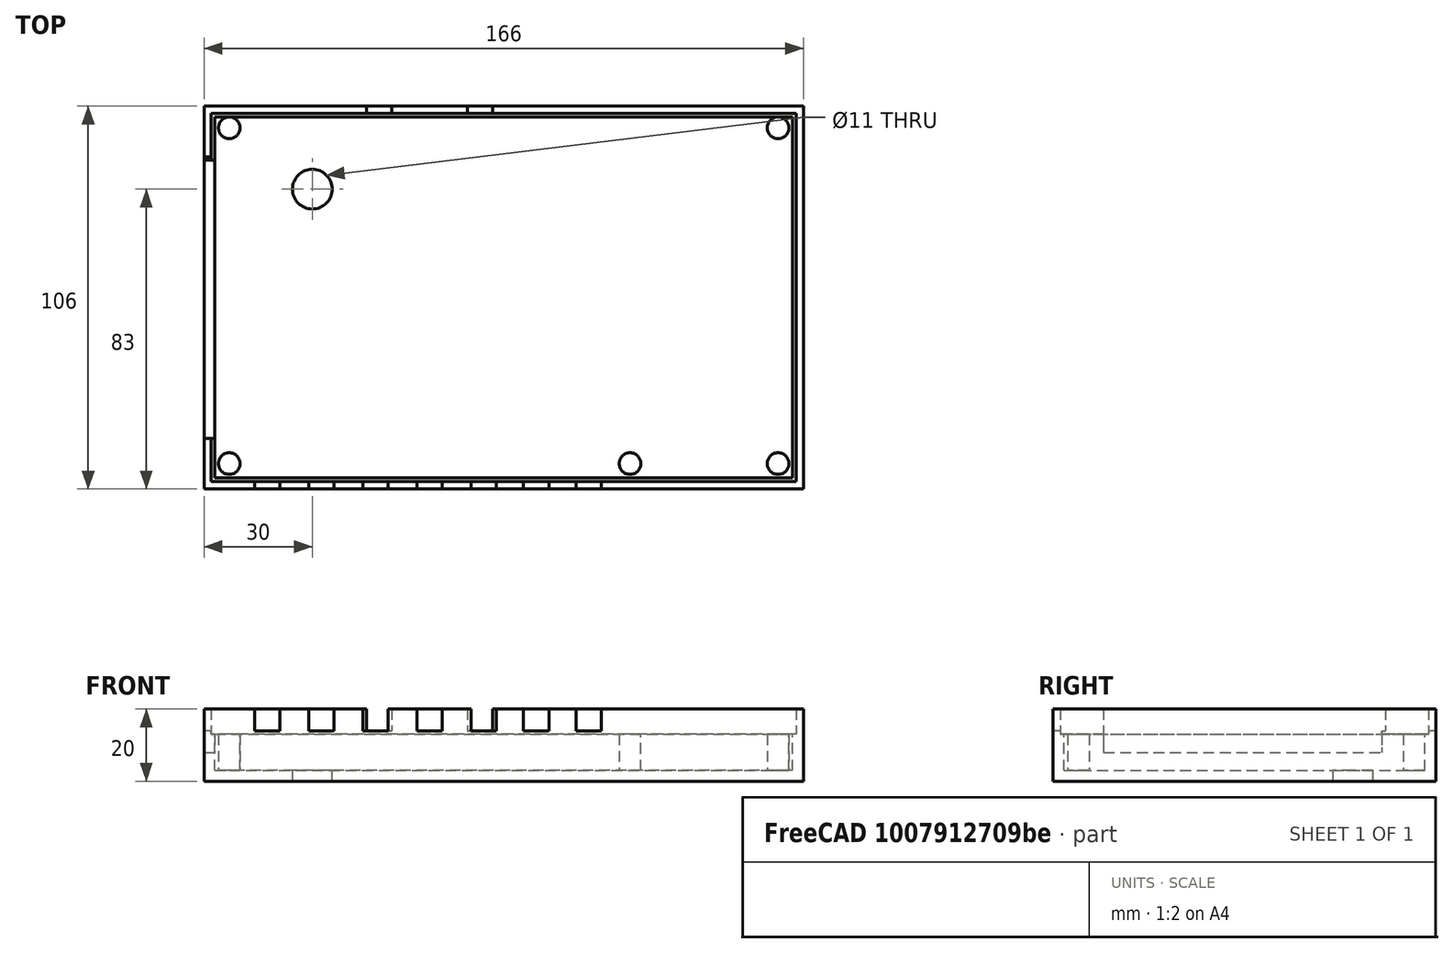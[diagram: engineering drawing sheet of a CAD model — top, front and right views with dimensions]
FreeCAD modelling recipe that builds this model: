
FCSTD DOCUMENT  (FreeCAD 1.0R39319 (Git))
Label: PLC14500-Nano-SupportV2
License: All rights reserved
LicenseURL: http://en.wikipedia.org/wiki/All_rights_reserved
objects: Sketcher::SketchObject×8, PartDesign::Pocket×5, PartDesign::Pad×3, App::DocumentObjectGroup×1, PartDesign::Body×1
note: 41 computed .brp shape members not serialized (recipe doc carries the construction recipe); baked Part::Feature solids carry a one-line shape summary decoded from their .brp

FEATURE [Sketcher::SketchObject] Sketch
  ArcFitTolerance = 0
  AttachmentSupport = -> [XY_Plane]
  FullyConstrained = true
  MakeInternals = false
  MapMode = 5
  sketch-geometry (4):
    g0: LineSegment StartX=-80 StartY=50 StartZ=0 EndX=80 EndY=50 EndZ=0
    g1: LineSegment StartX=80 StartY=50 StartZ=0 EndX=80 EndY=-50 EndZ=0
    g2: LineSegment StartX=80 StartY=-50 StartZ=0 EndX=-80 EndY=-50 EndZ=0
    g3: LineSegment StartX=-80 StartY=-50 StartZ=0 EndX=-80 EndY=50 EndZ=0
  constraints (10):
    c: Coincident(g0,g1)
    c: Coincident(g1,g2)
    c: Coincident(g2,g3)
    c: Coincident(g3,g0)
    c: Horizontal(g2)
    c: Vertical(g3)
    c: DistanceX(g0,g0) = 160
    c: DistanceY(g1,g1) = 100
    c: Symmetric(g0,g0,g-2)
    c: Symmetric(g0,g1,g-1)
FEATURE [PartDesign::Pad] Pad  label="Plate"
  Direction = (0,0,1)
  Length = 3
  Length2 = 100
  Profile = -> Sketch
  Suppressed = false
  Type = 0
FEATURE [Sketcher::SketchObject] Sketch001
  ArcFitTolerance = 0
  AttachmentSupport = -> [Pad]
  ExternalGeometry = -> [Pad]
  FullyConstrained = true
  MakeInternals = false
  MapMode = 5
  Placement = pos=(0,0,3) rot=(0,0,1;0rad)
  sketch-geometry (5):
    g0: Circle CenterX=-76 CenterY=47 CenterZ=0 NormalX=0 NormalY=0 NormalZ=1 AngleXU=0 Radius=3
    g1: Circle CenterX=76 CenterY=47 CenterZ=0 NormalX=0 NormalY=0 NormalZ=1 AngleXU=0 Radius=3
    g2: Circle CenterX=76 CenterY=-46 CenterZ=0 NormalX=0 NormalY=0 NormalZ=1 AngleXU=0 Radius=3
    g3: Circle CenterX=-76 CenterY=-46 CenterZ=0 NormalX=0 NormalY=0 NormalZ=1 AngleXU=0 Radius=3
    g4: Circle CenterX=35 CenterY=-46 CenterZ=0 NormalX=0 NormalY=0 NormalZ=1 AngleXU=0 Radius=3
  constraints (15):
    c: DistanceX(g-6,g0) = 4
    c: DistanceY(g0,g-6) = 3
    c: Radius(g0) = 3
    c: DistanceX(g1,g-4) = 4
    c: DistanceY(g1,g-4) = 3
    c: Radius(g1) = 3
    c: DistanceX(g2,g1) = 0
    c: DistanceX(g0,g3) = 0
    c: DistanceY(g-6,g3) = 4
    c: DistanceY(g-6,g4) = 4
    c: DistanceY(g-5,g2) = 4
    c: Radius(g3) = 3
    c: Radius(g4) = 3
    c: Radius(g2) = 3
    c: DistanceX(g4,g2) = 41
FEATURE [PartDesign::Pad] Pad001  label="BoardSupports"
  BaseFeature = -> Pad
  Direction = (0,0,1)
  Length = 10
  Length2 = 100
  Profile = -> Sketch001
  Suppressed = false
  Type = 0
FEATURE [Sketcher::SketchObject] Sketch002
  ArcFitTolerance = 1e-06
  AttachmentSupport = -> [XY_Plane]
  ExternalGeometry = -> [Pad001]
  FullyConstrained = true
  MakeInternals = false
  MapMode = 5
  sketch-geometry (8):
    g0: LineSegment StartX=-80 StartY=50 StartZ=0 EndX=-80 EndY=-50 EndZ=0
    g1: LineSegment StartX=-80 StartY=-50 StartZ=0 EndX=80 EndY=-50 EndZ=0
    g2: LineSegment StartX=80 StartY=-50 StartZ=0 EndX=80 EndY=50 EndZ=0
    g3: LineSegment StartX=80 StartY=50 StartZ=0 EndX=-80 EndY=50 EndZ=0
    g4: LineSegment StartX=-83 StartY=53 StartZ=0 EndX=-83 EndY=-53 EndZ=0
    g5: LineSegment StartX=-83 StartY=-53 StartZ=0 EndX=83 EndY=-53 EndZ=0
    g6: LineSegment StartX=83 StartY=-53 StartZ=0 EndX=83 EndY=53 EndZ=0
    g7: LineSegment StartX=83 StartY=53 StartZ=0 EndX=-83 EndY=53 EndZ=0
  constraints (22):
    c: Coincident(g0,g1)
    c: Coincident(g1,g2)
    c: Coincident(g2,g3)
    c: Coincident(g3,g0)
    c: Vertical(g0)
    c: Vertical(g2)
    c: Horizontal(g1)
    c: Horizontal(g3)
    c: Coincident(g2,g-3)
    c: Coincident(g0,g-5)
    c: Coincident(g4,g5)
    c: Coincident(g5,g6)
    c: Coincident(g6,g7)
    c: Coincident(g7,g4)
    c: Vertical(g4)
    c: Vertical(g6)
    c: Horizontal(g5)
    c: Horizontal(g7)
    c: DistanceY(g2,g6) = 3
    c: DistanceY(g5,g1) = 3
    c: DistanceX(g1,g5) = 3
    c: DistanceX(g4,g0) = 3
FEATURE [PartDesign::Pad] Pad002  label="Walls"
  BaseFeature = -> Pad001
  Direction = (0,0,1)
  Length = 20
  Length2 = 10
  Profile = -> Sketch002
  ReferenceAxis = -> Sketch002 [N_Axis]
  Refine = true
  Suppressed = false
  Type = 0
FEATURE [Sketcher::SketchObject] Sketch003
  ArcFitTolerance = 1e-06
  AttachmentOffset = pos=(0,0,20) rot=(0,0,1;0rad)
  AttachmentSupport = -> [XY_Plane]
  ExternalGeometry = -> [Pad002]
  FullyConstrained = true
  MakeInternals = false
  MapMode = 5
  Placement = pos=(0,0,20) rot=(0,0,1;0rad)
  sketch-geometry (40):
    g0: LineSegment StartX=-69 StartY=-51 StartZ=0 EndX=-69 EndY=-53 EndZ=0
    g1: LineSegment StartX=-69 StartY=-53 StartZ=0 EndX=-62 EndY=-53 EndZ=0
    g2: LineSegment StartX=-62 StartY=-53 StartZ=0 EndX=-62 EndY=-51 EndZ=0
    g3: LineSegment StartX=-62 StartY=-51 StartZ=0 EndX=-69 EndY=-51 EndZ=0
    g4: LineSegment StartX=-54 StartY=-51 StartZ=0 EndX=-54 EndY=-53 EndZ=0
    g5: LineSegment StartX=-54 StartY=-53 StartZ=0 EndX=-47 EndY=-53 EndZ=0
    g6: LineSegment StartX=-47 StartY=-53 StartZ=0 EndX=-47 EndY=-51 EndZ=0
    g7: LineSegment StartX=-47 StartY=-51 StartZ=0 EndX=-54 EndY=-51 EndZ=0
    g8: LineSegment StartX=-39 StartY=-51 StartZ=0 EndX=-39 EndY=-53 EndZ=0
    g9: LineSegment StartX=-39 StartY=-53 StartZ=0 EndX=-32 EndY=-53 EndZ=0
    g10: LineSegment StartX=-32 StartY=-53 StartZ=0 EndX=-32 EndY=-51 EndZ=0
    g11: LineSegment StartX=-32 StartY=-51 StartZ=0 EndX=-39 EndY=-51 EndZ=0
    g12: LineSegment StartX=-24 StartY=-51 StartZ=0 EndX=-24 EndY=-53 EndZ=0
    g13: LineSegment StartX=-24 StartY=-53 StartZ=0 EndX=-17 EndY=-53 EndZ=0
    g14: LineSegment StartX=-17 StartY=-53 StartZ=0 EndX=-17 EndY=-51 EndZ=0
    g15: LineSegment StartX=-17 StartY=-51 StartZ=0 EndX=-24 EndY=-51 EndZ=0
    g16: LineSegment StartX=-9 StartY=-51 StartZ=0 EndX=-9 EndY=-53 EndZ=0
    g17: LineSegment StartX=-9 StartY=-53 StartZ=0 EndX=-2 EndY=-53 EndZ=0
    g18: LineSegment StartX=-2 StartY=-53 StartZ=0 EndX=-2 EndY=-51 EndZ=0
    g19: LineSegment StartX=-2 StartY=-51 StartZ=0 EndX=-9 EndY=-51 EndZ=0
    g20: LineSegment StartX=5.5 StartY=-51 StartZ=0 EndX=5.5 EndY=-53 EndZ=0
    g21: LineSegment StartX=5.5 StartY=-53 StartZ=0 EndX=12.5 EndY=-53 EndZ=0
    g22: LineSegment StartX=12.5 StartY=-53 StartZ=0 EndX=12.5 EndY=-51 EndZ=0
    g23: LineSegment StartX=12.5 StartY=-51 StartZ=0 EndX=5.5 EndY=-51 EndZ=0
    g24: LineSegment StartX=20 StartY=-51 StartZ=0 EndX=20 EndY=-53 EndZ=0
    g25: LineSegment StartX=20 StartY=-53 StartZ=0 EndX=27 EndY=-53 EndZ=0
    g26: LineSegment StartX=27 StartY=-53 StartZ=0 EndX=27 EndY=-51 EndZ=0
    g27: LineSegment StartX=27 StartY=-51 StartZ=0 EndX=20 EndY=-51 EndZ=0
    g28: LineSegment StartX=-37 StartY=51 StartZ=0 EndX=-37 EndY=53 EndZ=0
    g29: LineSegment StartX=-37 StartY=53 StartZ=0 EndX=-30 EndY=53 EndZ=0
    g30: LineSegment StartX=-30 StartY=53 StartZ=0 EndX=-30 EndY=51 EndZ=0
    g31: LineSegment StartX=-30 StartY=51 StartZ=0 EndX=-37 EndY=51 EndZ=0
    g32: LineSegment StartX=-10 StartY=51 StartZ=0 EndX=-10 EndY=53 EndZ=0
    g33: LineSegment StartX=-10 StartY=53 StartZ=0 EndX=-3 EndY=53 EndZ=0
    g34: LineSegment StartX=-3 StartY=53 StartZ=0 EndX=-3 EndY=51 EndZ=0
    g35: LineSegment StartX=-3 StartY=51 StartZ=0 EndX=-10 EndY=51 EndZ=0
    g36: LineSegment StartX=-83 StartY=39 StartZ=0 EndX=-83 EndY=-39 EndZ=0
    g37: LineSegment StartX=-83 StartY=-39 StartZ=0 EndX=-81 EndY=-39 EndZ=0
    g38: LineSegment StartX=-81 StartY=-39 StartZ=0 EndX=-81 EndY=39 EndZ=0
    g39: LineSegment StartX=-81 StartY=39 StartZ=0 EndX=-83 EndY=39 EndZ=0
  constraints (120):
    c: Coincident(g0,g1)
    c: Coincident(g1,g2)
    c: Coincident(g2,g3)
    c: Coincident(g3,g0)
    c: Vertical(g0)
    c: Vertical(g2)
    c: Horizontal(g1)
    c: Horizontal(g3)
    c: DistanceX(g3,g3) = 7
    c: DistanceY(g2,g2) = 2
    c: DistanceX(g-5,g0) = 14
    c: PointOnObject(g0,g-3)
    c: Coincident(g4,g5)
    c: Coincident(g5,g6)
    c: Coincident(g6,g7)
    c: Coincident(g7,g4)
    c: Vertical(g4)
    c: Vertical(g6)
    c: Horizontal(g5)
    c: Horizontal(g7)
    c: Coincident(g8,g9)
    c: Coincident(g9,g10)
    c: Coincident(g10,g11)
    c: Coincident(g11,g8)
    c: Vertical(g8)
    c: Vertical(g10)
    c: Horizontal(g9)
    c: Horizontal(g11)
    c: Coincident(g12,g13)
    c: Coincident(g13,g14)
    c: Coincident(g14,g15)
    c: Coincident(g15,g12)
    c: Vertical(g12)
    c: Vertical(g14)
    c: Horizontal(g13)
    c: Horizontal(g15)
    c: Coincident(g16,g17)
    c: Coincident(g17,g18)
    c: Coincident(g18,g19)
    c: Coincident(g19,g16)
    c: Vertical(g16)
    c: Vertical(g18)
    c: Horizontal(g17)
    c: Horizontal(g19)
    c: Coincident(g20,g21)
    c: Coincident(g21,g22)
    c: Coincident(g22,g23)
    c: Coincident(g23,g20)
    c: Vertical(g20)
    c: Vertical(g22)
    c: Horizontal(g21)
    c: Horizontal(g23)
    c: Coincident(g24,g25)
    c: Coincident(g25,g26)
    c: Coincident(g26,g27)
    c: Coincident(g27,g24)
    c: Vertical(g24)
    c: Vertical(g26)
    c: Horizontal(g25)
    c: Horizontal(g27)
    c: Equal(g3,g7)
    c: Equal(g7,g11)
    c: Equal(g11,g15)
    c: Equal(g15,g19)
    c: Equal(g19,g23)
    c: Equal(g23,g27)
    c: Equal(g2,g4)
    c: Equal(g6,g8)
    c: Equal(g10,g12)
    c: Equal(g14,g16)
    c: Equal(g18,g20)
    c: PointOnObject(g4,g-3)
    c: PointOnObject(g8,g-3)
    c: PointOnObject(g12,g-3)
    c: PointOnObject(g16,g-3)
    c: PointOnObject(g20,g-3)
    c: PointOnObject(g24,g-3)
    c: Equal(g22,g24)
    c: DistanceX(g1,g5) = 15
    c: DistanceX(g5,g9) = 15
    c: DistanceX(g9,g13) = 15
    c: DistanceX(g13,g17) = 15
    c: DistanceX(g17,g21) = 14.5
    c: DistanceX(g21,g25) = 14.5
    c: Coincident(g28,g29)
    c: Coincident(g29,g30)
    c: Coincident(g30,g31)
    c: Coincident(g31,g28)
    c: Vertical(g28)
    c: Vertical(g30)
    c: Horizontal(g29)
    c: Horizontal(g31)
    c: Coincident(g32,g33)
    c: Coincident(g33,g34)
    c: Coincident(g34,g35)
    c: Coincident(g35,g32)
    c: Vertical(g32)
    c: Vertical(g34)
    c: Horizontal(g33)
    c: Horizontal(g35)
    c: Equal(g7,g29)
    c: Equal(g29,g33)
    c: Equal(g30,g32)
    c: Equal(g4,g28)
    c: DistanceX(g-6,g28) = 46
    c: DistanceX(g28,g32) = 27
    c: Coincident(g36,g37)
    c: Coincident(g37,g38)
    c: Coincident(g38,g39)
    c: Coincident(g39,g36)
    c: Vertical(g36)
    c: Vertical(g38)
    c: Horizontal(g37)
    c: Horizontal(g39)
    c: DistanceX(g39,g39) = 2
    c: PointOnObject(g36,g-5)
    c: DistanceY(g36,g-6) = 14
    c: PointOnObject(g28,g-6)
    c: PointOnObject(g32,g-6)
    c: DistanceY(g-5,g36) = 14
FEATURE [PartDesign::Pocket] Pocket  label="SideOpening"
  BaseFeature = -> Pad002
  Direction = (0,0,-1)
  Length = 30
  Length2 = 5
  Profile = -> Sketch003
  ReferenceAxis = -> Sketch003 [N_Axis]
  Refine = true
  Suppressed = false
  Type = 0
FEATURE [App::DocumentObjectGroup] Measurements
FEATURE [Sketcher::SketchObject] Sketch005
  ArcFitTolerance = 1e-06
  AttachmentSupport = -> [XY_Plane]
  FullyConstrained = true
  MakeInternals = false
  MapMode = 5
  sketch-geometry (1):
    g0: Circle CenterX=-53 CenterY=30 CenterZ=0 NormalX=0 NormalY=0 NormalZ=1 AngleXU=0 Radius=5.5
  constraints (3):
    c: DistanceX(g-3,g0) = 29
    c: DistanceY(g0,g-3) = 22
    c: Diameter(g0) = 11
FEATURE [Sketcher::SketchObject] Sketch004
  ArcFitTolerance = 1e-06
  AttachmentSupport = -> [Pocket]
  ExternalGeometry = -> [Pocket]
  FullyConstrained = true
  MakeInternals = false
  MapMode = 5
  Placement = pos=(0,0,14) rot=(0,0,1;0rad)
  sketch-geometry (4):
    g0: LineSegment StartX=-83 StartY=38 StartZ=0 EndX=-83 EndY=-39 EndZ=0
    g1: LineSegment StartX=-83 StartY=-39 StartZ=0 EndX=-80 EndY=-39 EndZ=0
    g2: LineSegment StartX=-80 StartY=-39 StartZ=0 EndX=-80 EndY=38 EndZ=0
    g3: LineSegment StartX=-80 StartY=38 StartZ=0 EndX=-83 EndY=38 EndZ=0
  constraints (10):
    c: Coincident(g0,g1)
    c: Coincident(g1,g2)
    c: Coincident(g2,g3)
    c: Coincident(g3,g0)
    c: Vertical(g0)
    c: Vertical(g2)
    c: Horizontal(g1)
    c: Horizontal(g3)
    c: Coincident(g2,g-4)
    c: Coincident(g0,g-3)
FEATURE [PartDesign::Pocket] Pocket001
  BaseFeature = -> Pocket
  Direction = (0,0,-1)
  Length = 6
  Length2 = 5
  Profile = -> Sketch004
  ReferenceAxis = -> Sketch004 [N_Axis]
  Refine = true
  Suppressed = false
  Type = 0
FEATURE [PartDesign::Pocket] Pocket002  label="ResetButton"
  BaseFeature = -> Pocket001
  Direction = (0,0,-1)
  Length = 5
  Length2 = 5
  Profile = -> Sketch005
  ReferenceAxis = -> Sketch005 [N_Axis]
  Refine = true
  Reversed = true
  Suppressed = false
  Type = 1
FEATURE [Sketcher::SketchObject] Sketch006
  ArcFitTolerance = 1e-06
  AttachmentOffset = pos=(0,0,20) rot=(0,0,1;0rad)
  AttachmentSupport = -> [XY_Plane]
  ExternalGeometry = -> [Pocket002]
  FullyConstrained = true
  MakeInternals = false
  MapMode = 5
  Placement = pos=(0,0,20) rot=(0,0,1;0rad)
  sketch-geometry (8):
    g0: LineSegment StartX=-80 StartY=50 StartZ=0 EndX=-80 EndY=-50 EndZ=0
    g1: LineSegment StartX=-80 StartY=-50 StartZ=0 EndX=80 EndY=-50 EndZ=0
    g2: LineSegment StartX=80 StartY=-50 StartZ=0 EndX=80 EndY=50 EndZ=0
    g3: LineSegment StartX=80 StartY=50 StartZ=0 EndX=-80 EndY=50 EndZ=0
    g4: LineSegment StartX=-81 StartY=51 StartZ=0 EndX=-81 EndY=-51 EndZ=0
    g5: LineSegment StartX=-81 StartY=-51 StartZ=0 EndX=81 EndY=-51 EndZ=0
    g6: LineSegment StartX=81 StartY=-51 StartZ=0 EndX=81 EndY=51 EndZ=0
    g7: LineSegment StartX=81 StartY=51 StartZ=0 EndX=-81 EndY=51 EndZ=0
  constraints (22):
    c: Coincident(g0,g1)
    c: Coincident(g1,g2)
    c: Coincident(g2,g3)
    c: Coincident(g3,g0)
    c: Vertical(g0)
    c: Vertical(g2)
    c: Horizontal(g1)
    c: Horizontal(g3)
    c: Coincident(g0,g-5)
    c: Coincident(g1,g-8)
    c: Coincident(g4,g5)
    c: Coincident(g5,g6)
    c: Coincident(g6,g7)
    c: Coincident(g7,g4)
    c: Vertical(g4)
    c: Vertical(g6)
    c: Horizontal(g5)
    c: Horizontal(g7)
    c: DistanceX(g2,g6) = 1
    c: DistanceX(g4,g0) = 1
    c: DistanceY(g5,g1) = 1
    c: DistanceY(g0,g4) = 1
FEATURE [PartDesign::Pocket] Pocket003  label="PCBRecess"
  BaseFeature = -> Pocket002
  Direction = (0,0,-1)
  Length = 7
  Length2 = 5
  Profile = -> Sketch006
  ReferenceAxis = -> Sketch006 [N_Axis]
  Refine = true
  Suppressed = false
  Type = 0
FEATURE [Sketcher::SketchObject] Sketch007
  ArcFitTolerance = 1e-06
  AttachmentSupport = -> [Pocket003]
  ExternalGeometry = -> [Pocket003]
  FullyConstrained = true
  MakeInternals = false
  MapMode = 5
  Placement = pos=(0,0,8) rot=(0,0,1;0rad)
  sketch-geometry (4):
    g0: LineSegment StartX=-83 StartY=38 StartZ=0 EndX=-83 EndY=-39 EndZ=0
    g1: LineSegment StartX=-83 StartY=-39 StartZ=0 EndX=-80 EndY=-39 EndZ=0
    g2: LineSegment StartX=-80 StartY=-39 StartZ=0 EndX=-80 EndY=38 EndZ=0
    g3: LineSegment StartX=-80 StartY=38 StartZ=0 EndX=-83 EndY=38 EndZ=0
  constraints (10):
    c: Coincident(g0,g1)
    c: Coincident(g1,g2)
    c: Coincident(g2,g3)
    c: Coincident(g3,g0)
    c: Vertical(g0)
    c: Vertical(g2)
    c: Horizontal(g1)
    c: Horizontal(g3)
    c: Coincident(g1,g-3)
    c: Coincident(g0,g-4)
FEATURE [PartDesign::Pocket] Pocket004  label="DeeperSidePocket"
  BaseFeature = -> Pocket003
  Direction = (1,1,1)
  Length = 5
  Length2 = 5
  Profile = -> Sketch007
  ReferenceAxis = -> Sketch007 [N_Axis]
  Refine = true
  Suppressed = false
  Type = 0
FEATURE [PartDesign::Body] Body  label="MainPlate"
  AllowCompound = false
  Group = -> [Sketch,Pad,Sketch001,Pad001,Sketch002,Pad002,Sketch003,Pocket,Sketch004,Pocket001,Sketch005,Pocket002,Sketch006,Pocket003,Sketch007,Pocket004]
  Origin = -> Origin
  Tip = -> Pocket004
